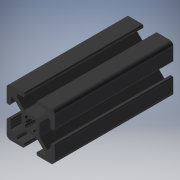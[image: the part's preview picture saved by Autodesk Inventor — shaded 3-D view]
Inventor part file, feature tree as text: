
AUTODESK INVENTOR PART (.ipt)
format: ipt  version: 2019 (Build 230136000, 136)  size: 235,520 bytes
history: native  units: mm
features: extrude x1, sketch x1
ambient origin geometry x8: Origin, YZ Plane, XZ Plane, XY Plane, X Axis, Y Axis, Z Axis, Center Point
bodies: Solid1 (feature_tree)
feature tree (2):
  extrude  "Extrusion1"  [1 undecoded]
  sketch  "Sketch_1"  dims[d0=50.0mm d1=0.0mm]
note: 1 required parameter value undecoded (feature->parameter linkage not recoverable at this tier; creation-order binding heuristic only, values carry confidence <= 0.55)
